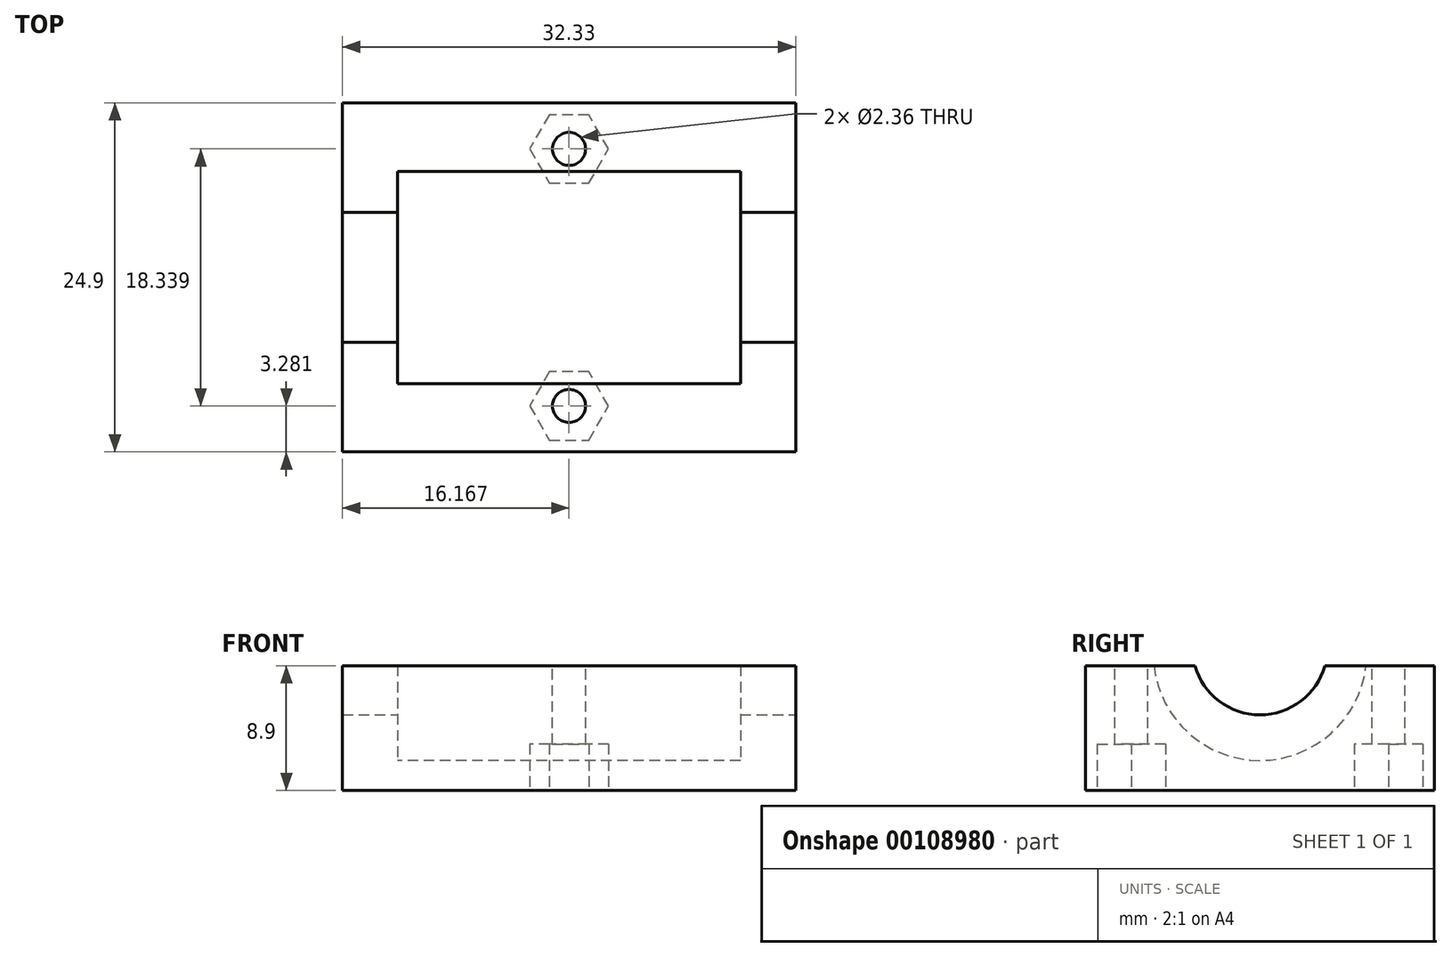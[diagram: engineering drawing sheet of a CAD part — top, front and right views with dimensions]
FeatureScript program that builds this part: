
annotation { "Feature Type Name" : "Feature", "Feature Type Description" : "" }
export const myFeature = defineFeature(function(context is Context, id is Id, definition is map)
    precondition{}
    {
        {
            var Q0;
            Q0=qCreatedBy(makeId("Right.planeOp"),FACE);
            var sketch = newSketch(context, id + "F0", { "sketchPlane" : qUnion([Q0])});
            skLineSegment(sketch, "E0.bottom", {"start": v(12.45, -4.44) * mm, "end": v(-12.45, -4.45) * mm});
            skLineSegment(sketch, "E0.top", {"start": v(12.45, 4.45) * mm, "end": v(-12.45, 4.44) * mm});
            skLineSegment(sketch, "E0.left", {"start": v(12.45, -4.44) * mm, "end": v(12.45, 4.45) * mm});
            skLineSegment(sketch, "E0.right", {"start": v(-12.45, -4.45) * mm, "end": v(-12.45, 4.44) * mm});
            skPoint(sketch, "E0.middle", {"position": v(0, 0) * mm});
            skSolve(sketch);
        }
        {
            var Q0;
            Q0 = qSketchRegion(id + "F0", true);
            extrude(context, id + "F1", {"entities" : qUnion([Q0]), "depth" : 3.94 * mm});
        }
        {
            var Q0;
            Q0=makeQuery(id+"F1.opExtrude","CAP_FACE",FACE,{"disambiguationData":[OSD([sQuery(id+"F0.wireOp",EDGE,"E0.bottom"),sQuery(id+"F0.wireOp",EDGE,"E0.top"),sQuery(id+"F0.wireOp",EDGE,"E0.left"),sQuery(id+"F0.wireOp",EDGE,"E0.right")])],"isStart":false});
            var sketch = newSketch(context, id + "F2", { "sketchPlane" : qUnion([Q0])});
            skLineSegment(sketch, "E1.bottom", {"start": v(-12.45, 4.45) * mm, "end": v(-7.57, 4.45) * mm});
            skLineSegment(sketch, "E1.top", {"start": v(-12.45, -4.44) * mm, "end": v(12.45, -4.44) * mm});
            skLineSegment(sketch, "E1.left", {"start": v(-12.45, 4.44) * mm, "end": v(-12.45, -4.44) * mm});
            skLineSegment(sketch, "E1.right", {"start": v(12.45, 4.45) * mm, "end": v(12.45, -4.44) * mm});
            skLineSegment(sketch, "E2.trimOffspring", {"start": v(7.57, 4.45) * mm, "end": v(12.45, 4.45) * mm});
            skArc(sketch, "E3", {"start": v(-7.57, 4.45) * mm, "mid": v(0, -2.31) * mm, "end": v(7.57, 4.45) * mm});
            skSolve(sketch);
        }
        {
            var Q0;
            Q0 = qSketchRegion(id + "F2", true);
            extrude(context, id + "F3", {"entities" : qUnion([Q0]), "operationType" : NewBodyOperationType.ADD, "depth" : 24.46 * mm});
        }
        {
            var Q0;
            Q0=makeQuery(id+"F3.opExtrude","CAP_FACE",FACE,{"disambiguationData":[OSD([sQuery(id+"F2.wireOp",EDGE,"E1.bottom"),sQuery(id+"F2.wireOp",EDGE,"E1.top"),sQuery(id+"F2.wireOp",EDGE,"E1.left"),sQuery(id+"F2.wireOp",EDGE,"E1.right"),sQuery(id+"F2.wireOp",EDGE,"TYnsB8ya-WYle-G6CB-24iZ-T6w1Zh2Edi8s"),sQuery(id+"F2.wireOp",EDGE,"8Qk2cRYJ-O90g-r4A9-VzlO-tEoDoWINZZq2"),sQuery(id+"F2.wireOp",EDGE,"Tx2M3oyi-r9D9-EWBA-TI7Q-Y03CfVB0JWJh"),sQuery(id+"F2.wireOp",EDGE,"E2.trimOffspring")])],"isStart":false});
            var sketch = newSketch(context, id + "F4", { "sketchPlane" : qUnion([Q0])});
            skLineSegment(sketch, "E4.bottom", {"start": v(-12.45, 4.44) * mm, "end": v(12.45, 4.44) * mm});
            skLineSegment(sketch, "E4.top", {"start": v(-12.45, -4.44) * mm, "end": v(12.45, -4.44) * mm});
            skLineSegment(sketch, "E4.left", {"start": v(-12.45, 4.44) * mm, "end": v(-12.45, -4.44) * mm});
            skLineSegment(sketch, "E4.right", {"start": v(12.45, 4.44) * mm, "end": v(12.45, -4.44) * mm});
            skSolve(sketch);
        }
        {
            var Q0;
            Q0 = qSketchRegion(id + "F4", true);
            extrude(context, id + "F5", {"entities" : qUnion([Q0]), "operationType" : NewBodyOperationType.ADD, "depth" : 3.94 * mm});
        }
        {
            var Q0;
            Q0=makeQuery(id+"F5.opExtrude","CAP_FACE",FACE,{"disambiguationData":[OSD([sQuery(id+"F4.wireOp",EDGE,"E4.bottom"),sQuery(id+"F4.wireOp",EDGE,"E4.top"),sQuery(id+"F4.wireOp",EDGE,"E4.left"),sQuery(id+"F4.wireOp",EDGE,"E4.right")])],"isStart":false});
            var sketch = newSketch(context, id + "F6", { "sketchPlane" : qUnion([Q0])});
            skCircle(sketch, "E5", {"center": v(0, 5.77) * mm, "radius": 4.83 * mm});
            skPoint(sketch, "E5.centerSnap0", {"position": v(0, 4.45) * mm});
            skSolve(sketch);
        }
        {
            var Q0;
            {var subQ0=sQuery(id+"F6.wireOp",EDGE,"E5");var subQ1=makeQuery(id+"F5.opExtrude","CAP_EDGE",EDGE,{"disambiguationData":[OSD([sQuery(id+"F4.wireOp",EDGE,"E4.bottom")])],"isStart":false});var subQ2=makeQuery(id+"F6.imprint","INTERSECT",VERTEX,{"disambiguationData":[OD(0.0)],"derivedFrom":[subQ1,subQ0]});Q0=makeQuery(id+"F6.imprint","IMPRINT",FACE,{"disambiguationData":[TD([[makeQuery(id+"F6.imprint","IMPRINT",EDGE,{"disambiguationData":[TD([[subQ2,1.0]])],"derivedFrom":subQ0}),1.0]])]});}
            extrude(context, id + "F7", {"entities" : qUnion([Q0]), "operationType" : NewBodyOperationType.REMOVE, "endBound" : BoundingType.THROUGH_ALL, "oppositeDirection" : true, "depth" : 25.4 * mm});
        }
        {
            var Q0;
            {var subQ3=sQuery(id+"F4.wireOp",EDGE,"E4.bottom");var subQ4=sQuery(id+"F0.wireOp",EDGE,"E0.right");var subQ6=sQuery(id+"F0.wireOp",EDGE,"E0.top");Q0=makeQuery(id+"F7.boolean.opBoolean","SPLIT",FACE,{"disambiguationData":[TD([makeQuery(id+"F1.opExtrude","SWEPT_FACE",FACE,{"disambiguationData":[OSD([subQ4])]})])],"derivedFrom":makeQuery(id+"F5.boolean.opBoolean","MERGE",FACE,{"derivedFrom":[makeQuery(id+"F3.boolean.opBoolean","MERGE",FACE,{"derivedFrom":[makeQuery(id+"F1.opExtrude","SWEPT_FACE",FACE,{"disambiguationData":[OSD([subQ6])]}),makeQuery(id+"F3.opExtrude","SWEPT_FACE",FACE,{"disambiguationData":[OSD([sQuery(id+"F2.wireOp",EDGE,"E1.bottom")])]}),makeQuery(id+"F3.opExtrude","SWEPT_FACE",FACE,{"disambiguationData":[OSD([sQuery(id+"F2.wireOp",EDGE,"E2.trimOffspring")])]})]}),makeQuery(id+"F5.opExtrude","SWEPT_FACE",FACE,{"disambiguationData":[OSD([subQ3])]})]})});}
            var sketch = newSketch(context, id + "F8", { "sketchPlane" : qUnion([Q0])});
            skCircle(sketch, "E6", {"center": v(16.17, -9.17) * mm, "radius": 1.18 * mm});
            skCircle(sketch, "E7", {"center": v(16.17, 9.17) * mm, "radius": 1.18 * mm});
            skSolve(sketch);
        }
        {
            var Q0;
            Q0 = qSketchRegion(id + "F8", true);
            extrude(context, id + "F9", {"entities" : qUnion([Q0]), "operationType" : NewBodyOperationType.REMOVE, "endBound" : BoundingType.THROUGH_ALL, "oppositeDirection" : true, "depth" : 25.4 * mm});
        }
        {
            var Q0;
            Q0=makeQuery(id+"F5.boolean.opBoolean","MERGE",FACE,{"derivedFrom":[makeQuery(id+"F3.boolean.opBoolean","MERGE",FACE,{"derivedFrom":[makeQuery(id+"F1.opExtrude","SWEPT_FACE",FACE,{"disambiguationData":[OSD([sQuery(id+"F0.wireOp",EDGE,"E0.bottom")])]}),makeQuery(id+"F3.opExtrude","SWEPT_FACE",FACE,{"disambiguationData":[OSD([sQuery(id+"F2.wireOp",EDGE,"E1.top")])]})]}),makeQuery(id+"F5.opExtrude","SWEPT_FACE",FACE,{"disambiguationData":[OSD([sQuery(id+"F4.wireOp",EDGE,"E4.top")])]})]});
            var sketch = newSketch(context, id + "F10", { "sketchPlane" : qUnion([Q0])});
            skCircle(sketch, "E8.cCircle", {"center": v(16.17, -9.17) * mm, "radius": 2.44 * mm, "construction": true});
            skLineSegment(sketch, "E8.0", {"start": v(13.35, -9.17) * mm, "end": v(14.76, -6.73) * mm});
            skLineSegment(sketch, "E8.1", {"start": v(14.76, -6.73) * mm, "end": v(17.57, -6.73) * mm});
            skLineSegment(sketch, "E8.2", {"start": v(17.57, -6.73) * mm, "end": v(18.98, -9.17) * mm});
            skLineSegment(sketch, "E8.3", {"start": v(18.98, -9.17) * mm, "end": v(17.57, -11.6) * mm});
            skLineSegment(sketch, "E8.4", {"start": v(17.57, -11.6) * mm, "end": v(14.76, -11.6) * mm});
            skLineSegment(sketch, "E8.5", {"start": v(14.76, -11.6) * mm, "end": v(13.35, -9.17) * mm});
            skPoint(sketch, "E8.0.midPoint", {"position": v(14.06, -7.95) * mm});
            skCircle(sketch, "E9.cCircle", {"center": v(16.17, 9.17) * mm, "radius": 2.44 * mm, "construction": true});
            skLineSegment(sketch, "E9.0", {"start": v(14.76, 6.73) * mm, "end": v(13.35, 9.17) * mm});
            skLineSegment(sketch, "E9.1", {"start": v(13.35, 9.17) * mm, "end": v(14.76, 11.6) * mm});
            skLineSegment(sketch, "E9.2", {"start": v(14.76, 11.6) * mm, "end": v(17.57, 11.6) * mm});
            skLineSegment(sketch, "E9.3", {"start": v(17.57, 11.6) * mm, "end": v(18.98, 9.17) * mm});
            skLineSegment(sketch, "E9.4", {"start": v(18.98, 9.17) * mm, "end": v(17.57, 6.73) * mm});
            skLineSegment(sketch, "E9.5", {"start": v(17.57, 6.73) * mm, "end": v(14.76, 6.73) * mm});
            skPoint(sketch, "E9.0.midPoint", {"position": v(14.06, 7.95) * mm});
            skSolve(sketch);
        }
        {
            var Q0;
            Q0 = qSketchRegion(id + "F10", true);
            extrude(context, id + "F11", {"entities" : qUnion([Q0]), "operationType" : NewBodyOperationType.REMOVE, "oppositeDirection" : true, "depth" : 3.3 * mm});
        }
    });
